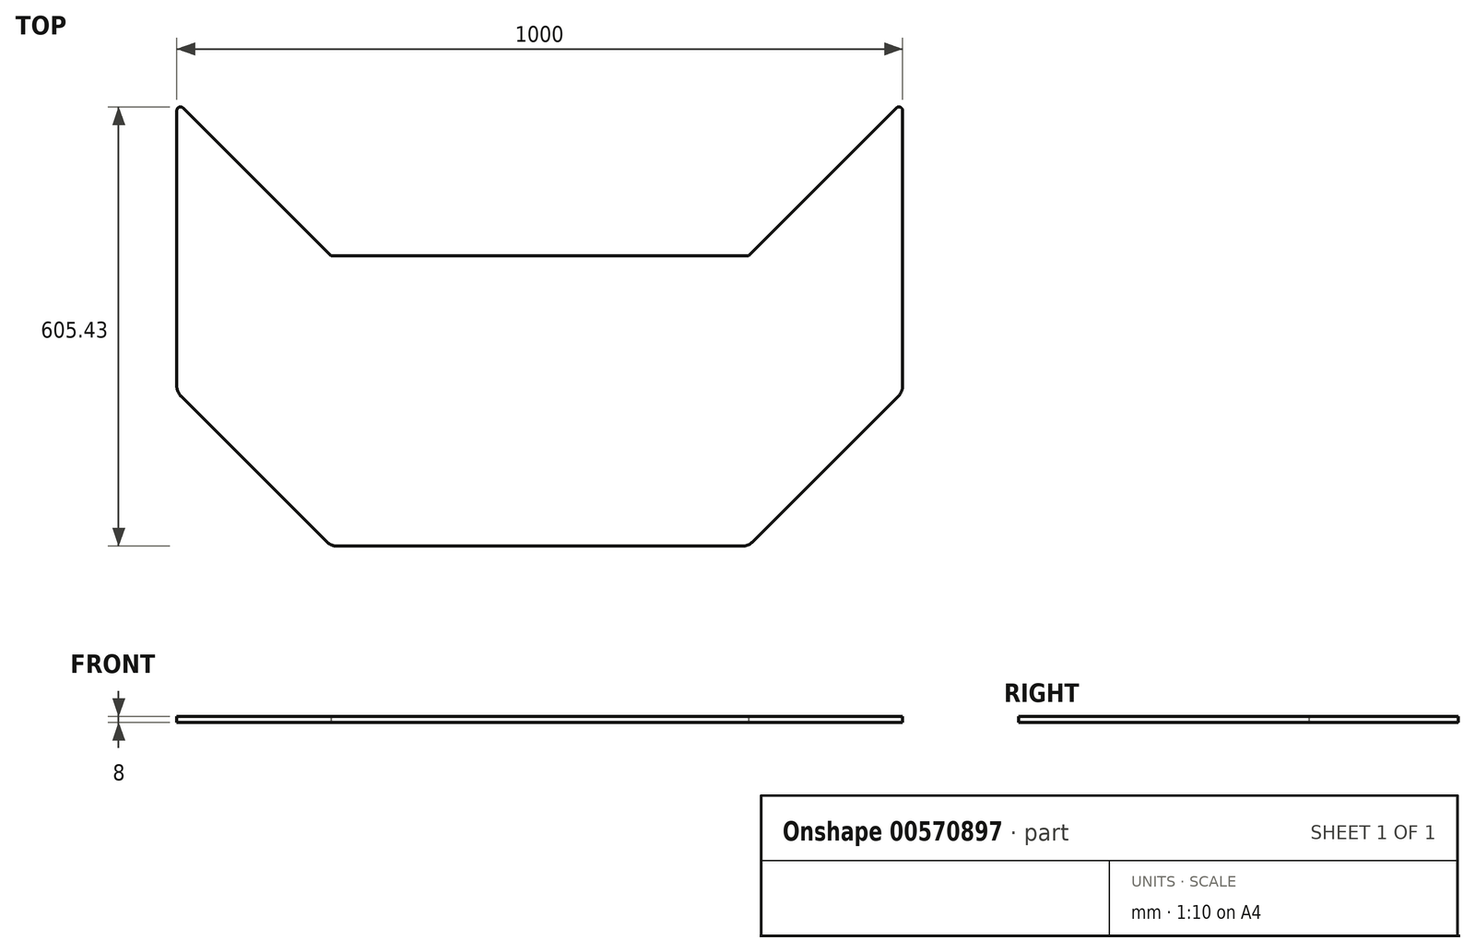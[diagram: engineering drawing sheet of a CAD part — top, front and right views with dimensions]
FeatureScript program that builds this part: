
annotation { "Feature Type Name" : "Feature", "Feature Type Description" : "" }
export const myFeature = defineFeature(function(context is Context, id is Id, definition is map)
    precondition{}
    {
        {
            var Q0;
            Q0=qCreatedBy(makeId("Top.planeOp"),FACE);
            var sketch = newSketch(context, id + "F0", { "sketchPlane" : qUnion([Q0])});
            skLineSegment(sketch, "E0", {"start": v(-287.5, 200) * mm, "end": v(287.5, 200) * mm});
            skLineSegment(sketch, "E1", {"start": v(287.5, 200) * mm, "end": v(491.46, 403.96) * mm});
            skLineSegment(sketch, "E2", {"start": v(500, 400.43) * mm, "end": v(500, 20.78) * mm});
            skLineSegment(sketch, "E3", {"start": v(279.22, -200) * mm, "end": v(-279.22, -200) * mm});
            skLineSegment(sketch, "E4", {"start": v(-500, 20.78) * mm, "end": v(-500, 400.43) * mm});
            skLineSegment(sketch, "E5", {"start": v(-491.46, 403.96) * mm, "end": v(-287.5, 200) * mm});
            skLineSegment(sketch, "E6", {"start": v(293.36, -194.14) * mm, "end": v(494.14, 6.64) * mm});
            skPoint(sketch, "E7.orphan", {"position": v(500, -200) * mm});
            skLineSegment(sketch, "E8", {"start": v(-494.14, 6.64) * mm, "end": v(-293.36, -194.14) * mm});
            skPoint(sketch, "E9.orphan", {"position": v(-500, -200) * mm});
            skLineSegment(sketch, "E10", {"start": v(-287.5, 200) * mm, "end": v(-287.5, -200) * mm, "construction": true});
            skLineSegment(sketch, "E11", {"start": v(287.5, 200) * mm, "end": v(287.5, -200) * mm, "construction": true});
            skPoint(sketch, "E12.visualSharp", {"position": v(-500, 412.5) * mm});
            skArc(sketch, "E12.filletArc", {"start": v(-491.46, 403.96) * mm, "mid": v(-496.91, 405.05) * mm, "end": v(-500, 400.43) * mm});
            skPoint(sketch, "E13.visualSharp", {"position": v(-500, 12.5) * mm});
            skArc(sketch, "E13.filletArc", {"start": v(-500, 20.78) * mm, "mid": v(-498.48, 13.13) * mm, "end": v(-494.14, 6.64) * mm});
            skPoint(sketch, "E14.visualSharp", {"position": v(-287.5, -200) * mm});
            skArc(sketch, "E14.filletArc", {"start": v(-293.36, -194.14) * mm, "mid": v(-286.87, -198.48) * mm, "end": v(-279.22, -200) * mm});
            skPoint(sketch, "E15.visualSharp", {"position": v(287.5, -200) * mm});
            skArc(sketch, "E15.filletArc", {"start": v(279.22, -200) * mm, "mid": v(286.87, -198.48) * mm, "end": v(293.36, -194.14) * mm});
            skPoint(sketch, "E16.visualSharp", {"position": v(500, 12.5) * mm});
            skArc(sketch, "E16.filletArc", {"start": v(494.14, 6.64) * mm, "mid": v(498.48, 13.13) * mm, "end": v(500, 20.78) * mm});
            skPoint(sketch, "E17.visualSharp", {"position": v(287.5, 200) * mm});
            skPoint(sketch, "E18.visualSharp", {"position": v(500, 412.5) * mm});
            skArc(sketch, "E18.filletArc", {"start": v(500, 400.43) * mm, "mid": v(496.91, 405.05) * mm, "end": v(491.46, 403.96) * mm});
            skSolve(sketch);
        }
        {
            var Q0;
            Q0 = qSketchRegion(id + "F0", true);
            extrude(context, id + "F1", {"entities" : qUnion([Q0]), "depth" : 8 * mm, "offsetDistance" : 25 * mm});
        }
    });
